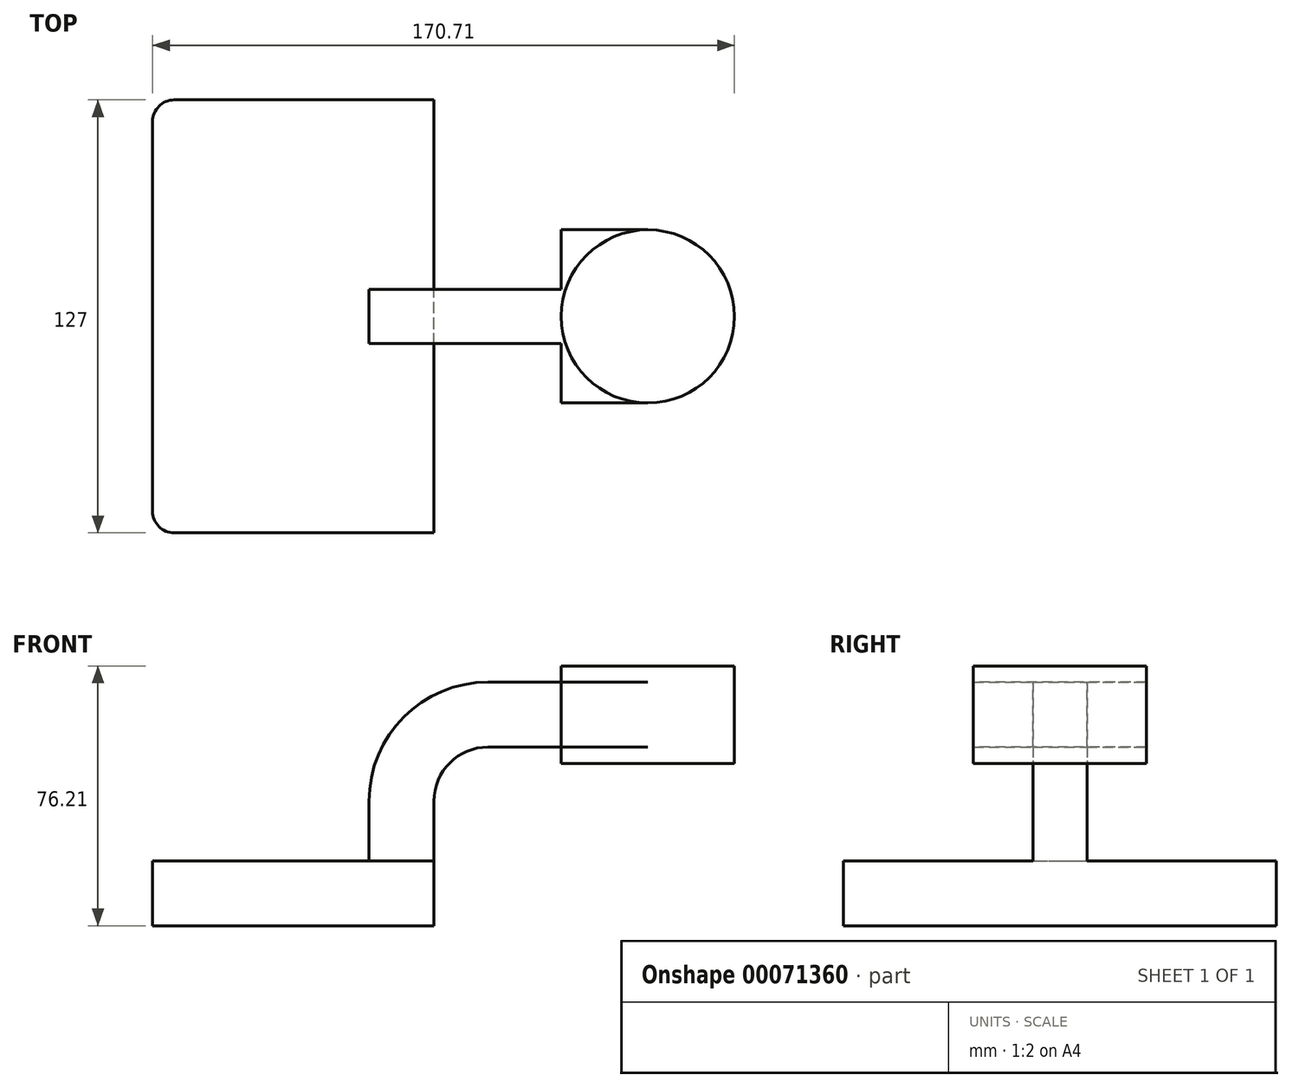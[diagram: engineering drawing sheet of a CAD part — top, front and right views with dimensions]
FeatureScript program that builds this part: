
annotation { "Feature Type Name" : "Feature", "Feature Type Description" : "" }
export const myFeature = defineFeature(function(context is Context, id is Id, definition is map)
    precondition{}
    {
        {
            var Q0;
            Q0=qCreatedBy(makeId("Front.planeOp"),FACE);
            var sketch = newSketch(context, id + "F0", { "sketchPlane" : qUnion([Q0])});
            skLineSegment(sketch, "E0.rect.bottom", {"start": v(41.28, -9.52) * mm, "end": v(-41.28, -9.53) * mm});
            skLineSegment(sketch, "E0.rect.top", {"start": v(41.27, 9.53) * mm, "end": v(-41.28, 9.53) * mm});
            skLineSegment(sketch, "E0.rect.left", {"start": v(41.27, -9.52) * mm, "end": v(41.27, 9.53) * mm});
            skLineSegment(sketch, "E0.rect.right", {"start": v(-41.28, -9.53) * mm, "end": v(-41.28, 9.53) * mm});
            skPoint(sketch, "E0.rect.middle", {"position": v(0, 0) * mm});
            skLineSegment(sketch, "E1.rect.bottom", {"start": v(129.44, 38.1) * mm, "end": v(78.64, 38.1) * mm});
            skLineSegment(sketch, "E1.rect.top", {"start": v(129.44, 66.68) * mm, "end": v(78.64, 66.68) * mm});
            skLineSegment(sketch, "E1.rect.left", {"start": v(129.44, 38.1) * mm, "end": v(129.44, 66.68) * mm});
            skLineSegment(sketch, "E1.rect.right", {"start": v(78.64, 38.1) * mm, "end": v(78.64, 66.68) * mm});
            skPoint(sketch, "E1.rect.middle", {"position": v(104.04, 52.39) * mm});
            skLineSegment(sketch, "E2", {"start": v(41.28, -9.52) * mm, "end": v(41.28, 27) * mm});
            skPoint(sketch, "E2.endSnap0", {"position": v(41.28, 0) * mm});
            skArc(sketch, "E3", {"start": v(41.28, 27) * mm, "mid": v(45.92, 38.23) * mm, "end": v(57.15, 42.88) * mm});
            skLineSegment(sketch, "E4", {"start": v(57.15, 42.88) * mm, "end": v(104.1, 42.88) * mm});
            skLineSegment(sketch, "E5.0", {"start": v(57.15, 61.93) * mm, "end": v(104.04, 61.93) * mm});
            skArc(sketch, "E5.1", {"start": v(22.23, 27) * mm, "mid": v(32.45, 51.7) * mm, "end": v(57.15, 61.93) * mm});
            skLineSegment(sketch, "E6", {"start": v(22.23, 27) * mm, "end": v(22.23, 9.53) * mm});
            skFitSpline(sketch, "E7", {"points": [v(-41.28, 9.53) * mm, v(57.15, 61.93) * mm], "startDerivative": vector(-4.18, 147.37) * mm, "endDerivative": vector(133.1, -0.65) * mm});
            skLineSegment(sketch, "E8", {"start": v(104.04, 66.68) * mm, "end": v(104.04, 38.1) * mm, "construction": true});
            skLineSegment(sketch, "E9", {"start": v(104.04, 66.68) * mm, "end": v(104.04, 38.1) * mm});
            skSolve(sketch);
        }
        {
            var Q0;
            {var subQ5=sQuery(id+"F0.wireOp",EDGE,"E0.rect.bottom");Q0=makeQuery(id+"F0.imprint","IMPRINT",FACE,{"disambiguationData":[TD([[makeQuery(id+"F0.imprint","IMPRINT",EDGE,{"derivedFrom":subQ5}),-1.0]])]});}
            extrude(context, id + "F1", {"entities" : qUnion([Q0]), "depth" : 127 * mm, "symmetric" : true});
        }
        {
            var Q0;
            {var subQ0=sQuery(id+"F0.wireOp",EDGE,"E3");Q0=makeQuery(id+"F0.imprint","IMPRINT",FACE,{"disambiguationData":[TD([[makeQuery(id+"F0.imprint","IMPRINT",EDGE,{"derivedFrom":subQ0}),1.0]])]});}
            var Q1;
            {var subQ0=sQuery(id+"F0.wireOp",EDGE,"E4");var subQ1=sQuery(id+"F0.wireOp",EDGE,"E1.rect.right");var subQ2=makeQuery(id+"F0.imprint","INTERSECT",VERTEX,{"derivedFrom":[subQ1,subQ0]});Q1=makeQuery(id+"F0.imprint","IMPRINT",FACE,{"disambiguationData":[TD([[makeQuery(id+"F0.imprint","IMPRINT",EDGE,{"disambiguationData":[TD([[subQ2,-1.0]])],"derivedFrom":subQ1}),-1.0]])]});}
            extrude(context, id + "F2", {"entities" : qUnion([Q0, Q1]), "operationType" : NewBodyOperationType.ADD, "depth" : 50.8 * mm, "symmetric" : true});
        }
        {
            var Q0;
            Q0=makeQuery(id+"F0.imprint","IMPRINT",FACE,{"disambiguationData":[TD([[makeQuery(id+"F0.imprint","IMPRINT",EDGE,{"derivedFrom":sQuery(id+"F0.wireOp",EDGE,"E5.1")}),1.0]])]});
            extrude(context, id + "F3", {"entities" : qUnion([Q0]), "operationType" : NewBodyOperationType.ADD, "depth" : 15.88 * mm, "symmetric" : true});
        }
        {
            var Q0;
            {var subQ0=sQuery(id+"F0.wireOp",EDGE,"E1.rect.left");Q0=makeQuery(id+"F0.imprint","IMPRINT",FACE,{"disambiguationData":[TD([[makeQuery(id+"F0.imprint","IMPRINT",EDGE,{"derivedFrom":subQ0}),1.0]])]});}
            var Q1;
            Q1=sQuery(id+"F0.wireOp",EDGE,"E9");
            revolve(context, id + "F4", {"operationType" : NewBodyOperationType.ADD, "entities" : qUnion([Q0]), "axis" : qUnion([Q1]), "revolveType" : RevolveType.FULL});
        }
        {
            var Q0;
            Q0=makeQuery(id+"F1.opExtrude","CAP_EDGE",EDGE,{"disambiguationData":[OSD([sQuery(id+"F0.wireOp",EDGE,"E2")])],"isStart":false});
            var Q1;
            Q1=makeQuery(id+"F1.opExtrude","CAP_EDGE",EDGE,{"disambiguationData":[OSD([sQuery(id+"F0.wireOp",EDGE,"E0.rect.right")])],"isStart":false});
            var Q2;
            Q2=makeQuery(id+"F1.opExtrude","CAP_EDGE",EDGE,{"disambiguationData":[OSD([sQuery(id+"F0.wireOp",EDGE,"E2")])],"isStart":true});
            var Q3;
            Q3=makeQuery(id+"F1.opExtrude","CAP_EDGE",EDGE,{"disambiguationData":[OSD([sQuery(id+"F0.wireOp",EDGE,"E0.rect.right")])],"isStart":true});
            fillet(context, id + "F5", {"entities" : qUnion([Q0, Q1, Q2, Q3]), "radius" : 6.35 * mm, "tangentPropagation" : true, "allowEdgeOverflow" : false});
        }
    });
